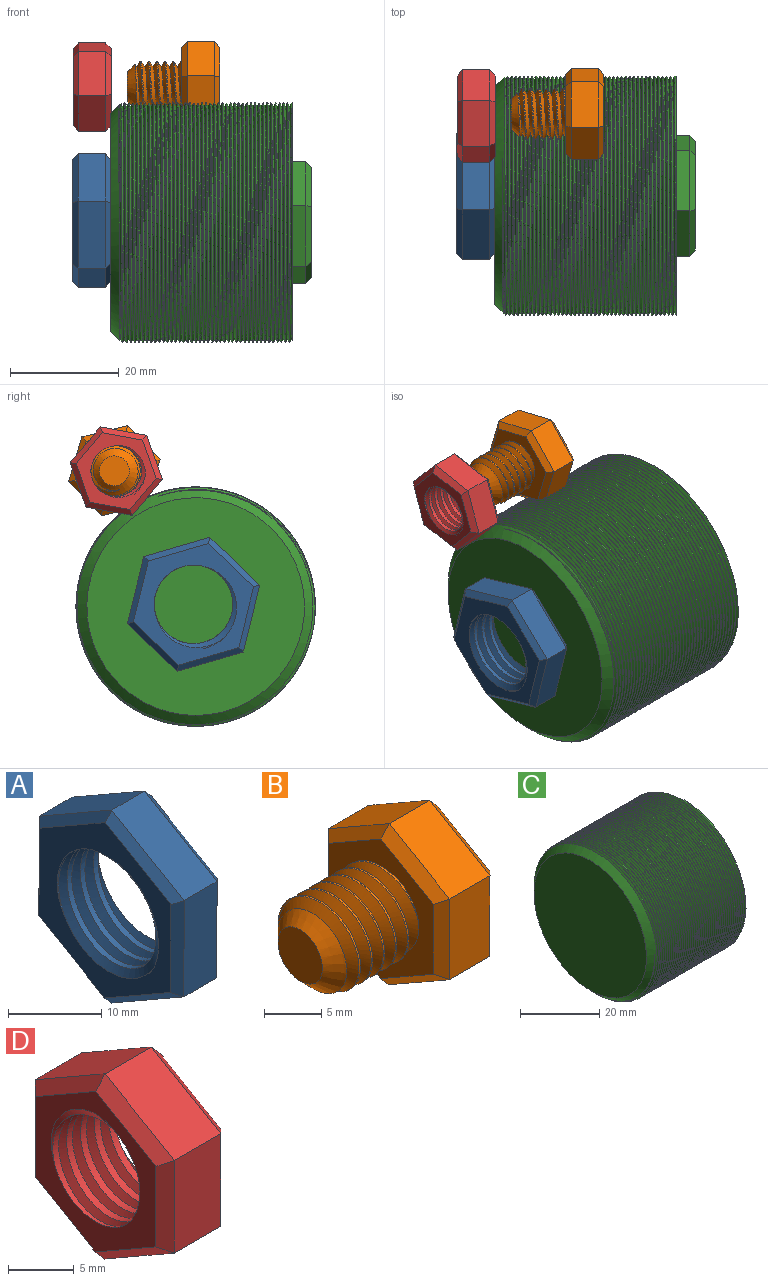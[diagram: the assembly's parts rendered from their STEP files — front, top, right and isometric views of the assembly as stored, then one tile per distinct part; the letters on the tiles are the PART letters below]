
ASSEMBLY  parts=4 mates=2
PART A: 23 faces, bbox 9.3x22.7x26 mm
  f0: cylinder r=7.24mm len=14.48mm, axis (1,0,0), area 111.6mm2, adj f7,f8,f21,f22
  f1: plane 10.98x6.38mm, normal (0,-0.5,0.86), area 63.5mm2, adj f2,f6,f14,f18
  f2: plane 12.7x5mm, normal (0,-1,0), area 63.5mm2, adj f1,f3,f12,f16
  f3: plane 11.02x6.32mm, normal (0,-0.5,-0.87), area 63.5mm2, adj f2,f4,f10,f15
  f4: plane 10.98x6.38mm, normal (0,0.5,-0.86), area 63.5mm2, adj f3,f5,f9,f17
  f5: plane 12.7x5mm, normal (0,1,0), area 63.5mm2, adj f4,f6,f11,f19
  f6: plane 11.02x6.32mm, normal (0,0.5,0.87), area 63.5mm2, adj f1,f5,f13,f20
  f7: plane 23.73x20.67mm, normal (-1,0,0), area 164.4mm2, adj f0,f9,f10,f11,f12,f13,f14,f21
  f8: plane 23.73x20.67mm, normal (1,0,0), area 164.4mm2, adj f0,f15,f16,f17,f18,f19,f20,f21
  f9: plane 10.99x6.96mm, normal (-0.71,0.36,-0.61), area 17.1mm2, adj f4,f7,f10,f11
  f10: plane 11.02x6.9mm, normal (-0.71,-0.35,-0.61), area 17.1mm2, adj f3,f7,f9,f12
  f11: plane 12.7x1.03mm, normal (-0.71,0.71,0), area 17.1mm2, adj f5,f7,f9,f13
  f12: plane 12.7x1.03mm, normal (-0.71,-0.71,0), area 17.1mm2, adj f2,f7,f10,f14
  f13: plane 11.02x6.9mm, normal (-0.71,0.35,0.61), area 17.1mm2, adj f6,f7,f11,f14
  f14: plane 10.99x6.96mm, normal (-0.71,-0.36,0.61), area 17.1mm2, adj f1,f7,f12,f13
  f15: plane 11.02x6.9mm, normal (0.71,-0.35,-0.61), area 17.1mm2, adj f3,f8,f16,f17
  f16: plane 12.7x1.03mm, normal (0.71,-0.71,0), area 17.1mm2, adj f2,f8,f15,f18
  f17: plane 10.99x6.96mm, normal (0.71,0.36,-0.61), area 17.1mm2, adj f4,f8,f15,f19
  f18: plane 10.99x6.96mm, normal (0.71,-0.36,0.61), area 17.1mm2, adj f1,f8,f16,f20
  f19: plane 12.7x1.03mm, normal (0.71,0.71,0), area 17.1mm2, adj f5,f8,f17,f20
  f20: plane 11.02x6.9mm, normal (0.71,0.35,0.61), area 17.1mm2, adj f6,f8,f18,f19
  f21: bspline ~19.31x16.73mm, area 223mm2, adj f0,f7,f8,f22
  f22: bspline ~19.31x16.73mm, area 223mm2, adj f0,f7,f8,f21
PART B: 25 faces, bbox 17.8x15.9x18.1 mm
  f0: cylinder r=4.75mm len=9.5mm, axis (1,0,0), area 28.1mm2, adj f1,f2,f4,f12
  f1: bspline ~10.97x9.91mm, area 196.7mm2, adj f0,f2,f4,f12
  f2: bspline ~10.97x10.66mm, area 196.6mm2, adj f0,f1,f4,f12
  f3: plane 5.5x5.5mm, normal (-1,0,0), area 23.8mm2, adj f4
  f4: cone r=4.75mm half-angle=45deg, axis (1,0,0), area 47.4mm2, adj f0,f1,f2,f3
  f5: plane 7.48x5mm, normal (0,-0.5,0.86), area 43.3mm2, adj f6,f10,f18,f22
  f6: plane 8.66x5mm, normal (0,-1,0), area 43.3mm2, adj f5,f7,f16,f20
  f7: plane 7.52x5mm, normal (0,-0.5,-0.87), area 43.3mm2, adj f6,f8,f14,f19
  f8: plane 7.48x5mm, normal (0,0.5,-0.86), area 43.3mm2, adj f7,f9,f13,f21
  f9: plane 8.66x5mm, normal (0,1,0), area 43.3mm2, adj f8,f10,f15,f23
  f10: plane 7.52x5mm, normal (0,0.5,0.87), area 43.3mm2, adj f5,f9,f17,f24
  f11: plane 15.01x13.03mm, normal (1,0,0), area 146.4mm2, adj f13,f14,f15,f16,f17,f18
  f12: plane 15.83x13.85mm, normal (-1,0,0), area 89.2mm2, adj f0,f1,f2,f19,f20,f21,f22,f23
  f13: plane 7.49x4.93mm, normal (0.71,0.36,-0.61), area 11.4mm2, adj f8,f11,f14,f15
  f14: plane 7.52x4.88mm, normal (0.71,-0.35,-0.61), area 11.4mm2, adj f7,f11,f13,f16
  f15: plane 8.66x1.03mm, normal (0.71,0.71,0), area 11.4mm2, adj f9,f11,f13,f17
  f16: plane 8.66x1.03mm, normal (0.71,-0.71,0), area 11.4mm2, adj f6,f11,f14,f18
  f17: plane 7.52x4.88mm, normal (0.71,0.35,0.61), area 11.4mm2, adj f10,f11,f15,f18
  f18: plane 7.49x4.93mm, normal (0.71,-0.36,0.61), area 11.4mm2, adj f5,f11,f16,f17
  f19: plane 7.52x4.88mm, normal (-0.71,-0.35,-0.61), area 11.4mm2, adj f7,f12,f20,f21
  f20: plane 8.66x1.03mm, normal (-0.71,-0.71,0), area 11.4mm2, adj f6,f12,f19,f22
  f21: plane 7.49x4.93mm, normal (-0.71,0.36,-0.61), area 11.4mm2, adj f8,f12,f19,f23
  f22: plane 7.49x4.93mm, normal (-0.71,-0.36,0.61), area 11.4mm2, adj f5,f12,f20,f24
  f23: plane 8.66x1.03mm, normal (-0.71,0.71,0), area 11.4mm2, adj f9,f12,f21,f24
  f24: plane 7.52x4.88mm, normal (-0.71,0.35,0.61), area 11.4mm2, adj f10,f12,f22,f23
PART C: 21 faces, bbox 37x50.9x44.1 mm
  f0: cylinder r=22.05mm len=44.1mm, axis (1,0,0), area 1030.6mm2, adj f2,f3,f4,f5,f6,f7
  f1: plane 40.1x40.1mm, normal (-1,0,0), area 1262.9mm2, adj f3
  f2: plane 44.1x43.86mm, normal (1,0,0), area 1163.9mm2, adj f0,f5,f6,f8,f9,f10,f11,f12
  f3: cone r=22.05mm half-angle=45deg, axis (1,0,0), area 325.1mm2, adj f0,f1,f4,f6,f7
  f4: cone r=22.05mm half-angle=45deg, axis (1,0,0), area 0.7mm2, adj f0,f3,f6
  f5: plane 0.57x0.33mm, normal (0,1,0), area 0.1mm2, adj f0,f2,f7
  f6: bspline ~50.92x44.1mm, area 3810.3mm2, adj f0,f2,f3,f4,f7
  f7: bspline ~50.92x44.1mm, area 3778.1mm2, adj f0,f3,f5,f6
  f8: plane 9.98x5.81mm, normal (0,-0.5,0.86), area 28.9mm2, adj f2,f9,f13,f20
  f9: plane 11.55x2.5mm, normal (0,-1,0), area 28.9mm2, adj f2,f8,f10,f18
  f10: plane 10.02x5.74mm, normal (0,-0.5,-0.87), area 28.9mm2, adj f2,f9,f11,f16
  f11: plane 9.98x5.81mm, normal (0,0.5,-0.86), area 28.9mm2, adj f2,f10,f12,f15
  f12: plane 11.55x2.5mm, normal (0,1,0), area 28.9mm2, adj f2,f11,f13,f17
  f13: plane 10.02x5.74mm, normal (0,0.5,0.87), area 28.9mm2, adj f2,f8,f12,f19
  f14: plane 20.78x18.04mm, normal (1,0,0), area 280.6mm2, adj f15,f16,f17,f18,f19,f20
  f15: plane 9.98x6.38mm, normal (0.71,0.36,-0.61), area 15.5mm2, adj f11,f14,f16,f17
  f16: plane 10.02x6.32mm, normal (0.71,-0.35,-0.61), area 15.5mm2, adj f10,f14,f15,f18
  f17: plane 11.55x1.04mm, normal (0.71,0.71,0), area 15.5mm2, adj f12,f14,f15,f19
  f18: plane 11.55x1.04mm, normal (0.71,-0.71,0), area 15.5mm2, adj f9,f14,f16,f20
  f19: plane 10.02x6.32mm, normal (0.71,0.35,0.61), area 15.5mm2, adj f13,f14,f17,f20
  f20: plane 9.98x6.38mm, normal (0.71,-0.36,0.61), area 15.5mm2, adj f8,f14,f18,f19
PART D: 23 faces, bbox 9.1x15.4x17.7 mm
  f0: plane 7.49x5mm, normal (0,-0.5,0.86), area 43.3mm2, adj f1,f5,f13,f17
  f1: plane 8.66x5mm, normal (0,-1,0), area 43.3mm2, adj f0,f2,f11,f15
  f2: plane 7.51x5mm, normal (0,-0.5,-0.87), area 43.3mm2, adj f1,f3,f9,f14
  f3: plane 7.49x5mm, normal (0,0.5,-0.86), area 43.3mm2, adj f2,f4,f8,f16
  f4: plane 8.66x5mm, normal (0,1,0), area 43.3mm2, adj f3,f5,f10,f18
  f5: plane 7.51x5mm, normal (0,0.5,0.87), area 43.3mm2, adj f0,f4,f12,f19
  f6: plane 15.37x13.38mm, normal (-1,0,0), area 71.4mm2, adj f8,f9,f10,f11,f12,f13,f20,f21
  f7: plane 15.37x13.38mm, normal (1,0,0), area 71.4mm2, adj f14,f15,f16,f17,f18,f19,f20,f21
  f8: plane 7.49x4.93mm, normal (-0.71,0.36,-0.61), area 11.4mm2, adj f3,f6,f9,f10
  f9: plane 7.51x4.89mm, normal (-0.71,-0.35,-0.61), area 11.4mm2, adj f2,f6,f8,f11
  f10: plane 8.66x1.02mm, normal (-0.71,0.71,0), area 11.4mm2, adj f4,f6,f8,f12
  f11: plane 8.66x1.02mm, normal (-0.71,-0.71,0), area 11.4mm2, adj f1,f6,f9,f13
  f12: plane 7.51x4.89mm, normal (-0.71,0.35,0.61), area 11.4mm2, adj f5,f6,f10,f13
  f13: plane 7.49x4.93mm, normal (-0.71,-0.36,0.61), area 11.4mm2, adj f0,f6,f11,f12
  f14: plane 7.51x4.89mm, normal (0.71,-0.35,-0.61), area 11.4mm2, adj f2,f7,f15,f16
  f15: plane 8.66x1.02mm, normal (0.71,-0.71,0), area 11.4mm2, adj f1,f7,f14,f17
  f16: plane 7.49x4.93mm, normal (0.71,0.36,-0.61), area 11.4mm2, adj f3,f7,f14,f18
  f17: plane 7.49x4.93mm, normal (0.71,-0.36,0.61), area 11.4mm2, adj f0,f7,f15,f19
  f18: plane 8.66x1.02mm, normal (0.71,0.71,0), area 11.4mm2, adj f4,f7,f16,f19
  f19: plane 7.51x4.89mm, normal (0.71,0.35,0.61), area 11.4mm2, adj f5,f7,f17,f18
  f20: cylinder r=4.66mm len=9.32mm, axis (1,0,0), area 85.4mm2, adj f6,f7,f21,f22
  f21: bspline ~12.5x10.82mm, area 128.4mm2, adj f6,f7,f20,f22
  f22: bspline ~12.5x10.82mm, area 128.5mm2, adj f6,f7,f20,f21
PLACE A rot(axis=(0,0.6,-0.8),180deg) t=(-55.27,-6.86,23.48)mm fixed
PLACE B rot(axis=(-1,0,0),43.8deg) t=(-31.66,7.73,48.08)mm
PLACE C rot(axis=(-1,0,0),106.1deg) t=(-14.77,-7.25,23.06)mm
PLACE D rot(axis=(1,0,0),100.2deg) t=(-48.16,7.38,48.02)mm fixed
MATE cylindrical C.f0 <-> A.f7  axis (-1,0,0) through (-48.27,-7.25,23.06)mm
MATE cylindrical B.f0 <-> D.f6  axis (-1,0,0) through (-45.16,7.73,48.08)mm
